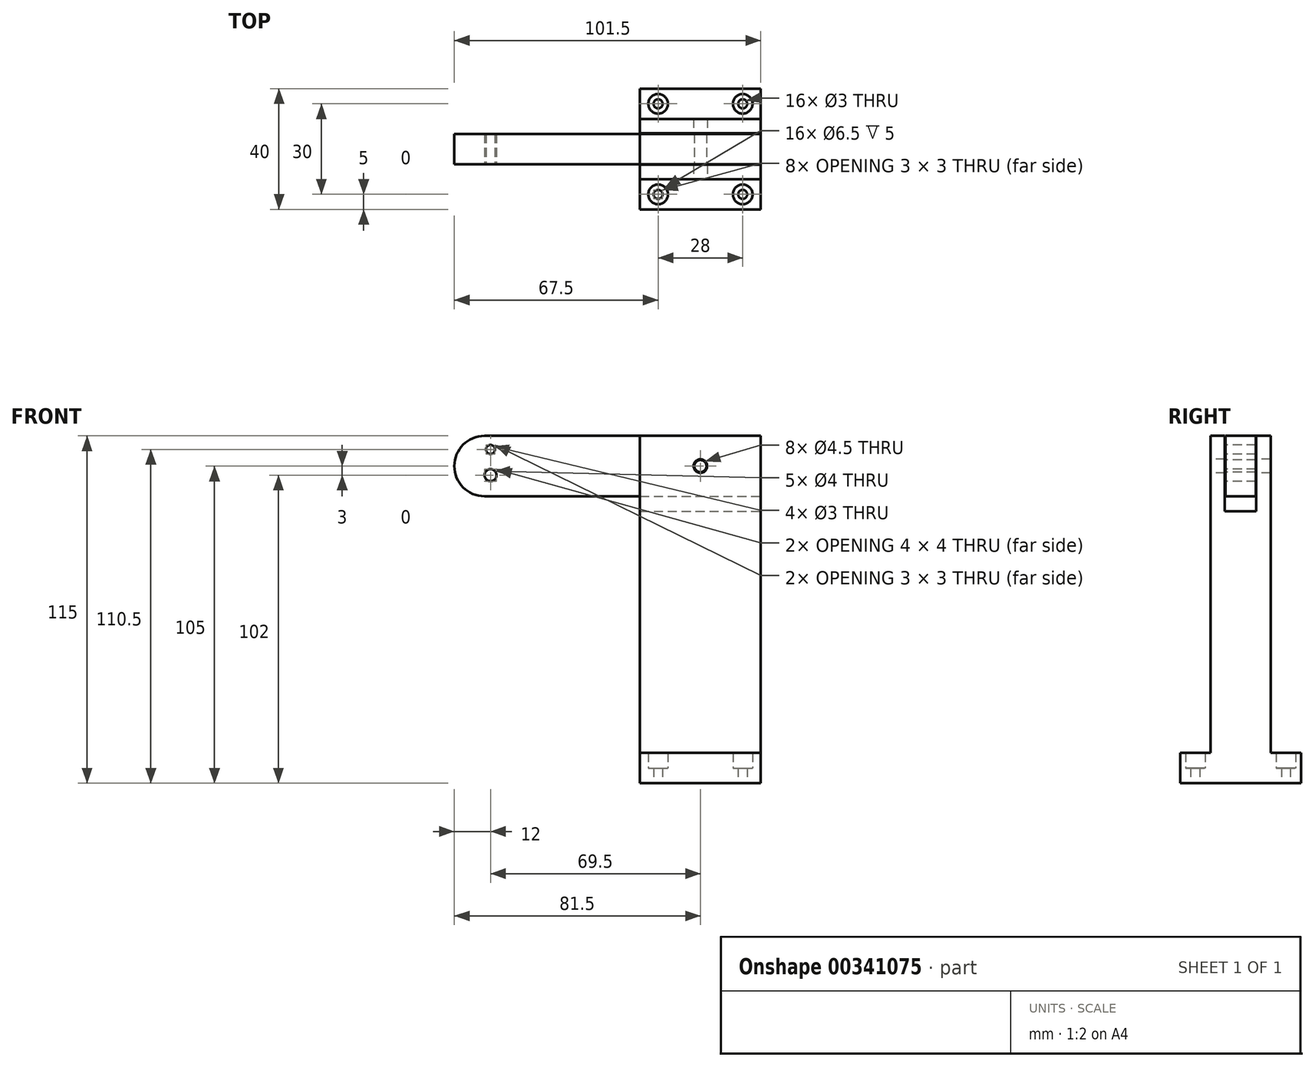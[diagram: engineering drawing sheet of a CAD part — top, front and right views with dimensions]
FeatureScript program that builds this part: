
annotation { "Feature Type Name" : "Feature", "Feature Type Description" : "" }
export const myFeature = defineFeature(function(context is Context, id is Id, definition is map)
    precondition{}
    {
        {
            var Q0;
            Q0=qCreatedBy(makeId("Top.planeOp"),FACE);
            var sketch = newSketch(context, id + "F0", { "sketchPlane" : qUnion([Q0])});
            skLineSegment(sketch, "E0.bottom", {"start": v(51.5, 0) * mm, "end": v(91.5, 0) * mm});
            skLineSegment(sketch, "E0.top", {"start": v(51.5, 40) * mm, "end": v(91.5, 40) * mm});
            skLineSegment(sketch, "E0.left", {"start": v(51.5, 0) * mm, "end": v(51.5, 40) * mm});
            skLineSegment(sketch, "E0.right", {"start": v(91.5, 0) * mm, "end": v(91.5, 40) * mm});
            skSolve(sketch);
        }
        {
            var Q0;
            Q0=qSketchRegion(id+"F0",true);
            extrude(context, id + "F1", {"entities" : qUnion([Q0]), "depth" : (95 + 20) * mm});
        }
        {
            var Q0;
            Q0=makeQuery(id+"F1.opExtrude","CAP_FACE",FACE,{"disambiguationData":[OSD([sQuery(id+"F0.wireOp",EDGE,"E0.bottom"),sQuery(id+"F0.wireOp",EDGE,"E0.top"),sQuery(id+"F0.wireOp",EDGE,"E0.left"),sQuery(id+"F0.wireOp",EDGE,"E0.right")])],"isStart":false});
            var sketch = newSketch(context, id + "F2", { "sketchPlane" : qUnion([Q0])});
            skLineSegment(sketch, "E1.bottom", {"start": v(51.5, 0) * mm, "end": v(91.5, 0) * mm});
            skLineSegment(sketch, "E1.top", {"start": v(51.5, 10) * mm, "end": v(91.5, 10) * mm});
            skLineSegment(sketch, "E1.left", {"start": v(51.5, 0) * mm, "end": v(51.5, 10) * mm});
            skLineSegment(sketch, "E1.right", {"start": v(91.5, 0) * mm, "end": v(91.5, 10) * mm});
            skLineSegment(sketch, "E2", {"start": v(51.5, 20) * mm, "end": v(91.5, 20) * mm, "construction": true});
            skLineSegment(sketch, "E3.MirrorCS", {"start": v(51.5, 30) * mm, "end": v(91.5, 30) * mm});
            skLineSegment(sketch, "E4.MirrorCS", {"start": v(51.5, 40) * mm, "end": v(51.5, 30) * mm});
            skLineSegment(sketch, "E5.MirrorCS", {"start": v(51.5, 40) * mm, "end": v(91.5, 40) * mm});
            skLineSegment(sketch, "E6.MirrorCS", {"start": v(91.5, 40) * mm, "end": v(91.5, 30) * mm});
            skSolve(sketch);
        }
        {
            var Q0;
            Q0=qSketchRegion(id+"F2",true);
            extrude(context, id + "F3", {"entities" : qUnion([Q0]), "operationType" : NewBodyOperationType.REMOVE, "oppositeDirection" : true, "depth" : (115 - 10) * mm});
        }
        {
            var Q0;
            Q0=makeQuery(id+"F3.boolean.opBoolean","COPY",FACE,{"derivedFrom":makeQuery(id+"F3.opExtrude","CAP_FACE",FACE,{"disambiguationData":[OSD([sQuery(id+"F2.wireOp",EDGE,"E1.bottom"),sQuery(id+"F2.wireOp",EDGE,"E1.top"),sQuery(id+"F2.wireOp",EDGE,"E1.left"),sQuery(id+"F2.wireOp",EDGE,"E1.right")])],"isStart":false})});
            var sketch = newSketch(context, id + "F4", { "sketchPlane" : qUnion([Q0])});
            skLineSegment(sketch, "E7", {"start": v(51.5, 20) * mm, "end": v(91.5, 20) * mm, "construction": true});
            skLineSegment(sketch, "E8", {"start": v(51.5, 20) * mm, "end": v(51.5, 35) * mm, "construction": true});
            skLineSegment(sketch, "E9", {"start": v(51.5, 35) * mm, "end": v(57.5, 35) * mm, "construction": true});
            skPoint(sketch, "E10", {"position": v(57.5, 35) * mm});
            skLineSegment(sketch, "E11", {"start": v(71.5, 20) * mm, "end": v(71.5, 42.68) * mm, "construction": true});
            skPoint(sketch, "E11.endSnap0", {"position": v(71.5, 30) * mm});
            skPoint(sketch, "E12.MirrorP", {"position": v(85.5, 35) * mm});
            skPoint(sketch, "E13.MirrorP", {"position": v(85.5, 5) * mm});
            skPoint(sketch, "E14.MirrorP", {"position": v(57.5, 5) * mm});
            skSolve(sketch);
        }
        {
            var Q0;
            Q0=sQuery(id+"F4.wireOp",VERTEX,"E14.MirrorP");
            var Q1;
            Q1=sQuery(id+"F4.wireOp",VERTEX,"E13.MirrorP");
            var Q2;
            Q2=sQuery(id+"F4.wireOp",VERTEX,"E12.MirrorP");
            var Q3;
            Q3=sQuery(id+"F4.wireOp",VERTEX,"E10");
            var Q4;
            Q4=makeQuery(id+"F1.opExtrude","SWEPT_BODY",BODY,{"disambiguationData":[OSD([sQuery(id+"F0.wireOp",EDGE,"E0.bottom"),sQuery(id+"F0.wireOp",EDGE,"E0.top"),sQuery(id+"F0.wireOp",EDGE,"E0.left"),sQuery(id+"F0.wireOp",EDGE,"E0.right")])]});
            hole(context, id + "F5", {"style" : HoleStyle.C_BORE, "endStyle" : HoleEndStyle.BLIND, "holeDiameter" : 3 * mm, "cBoreDiameter" : 6.5 * mm, "cBoreDepth" : 5 * mm, "holeDepth" : (10.4 + .3) * mm, "locations" : qUnion([Q0, Q1, Q2, Q3]), "scope" : qUnion([Q4])});
        }
        {
            var Q0;
            Q0=makeQuery(id+"F1.opExtrude","CAP_FACE",FACE,{"disambiguationData":[OSD([sQuery(id+"F0.wireOp",EDGE,"E0.bottom"),sQuery(id+"F0.wireOp",EDGE,"E0.top"),sQuery(id+"F0.wireOp",EDGE,"E0.left"),sQuery(id+"F0.wireOp",EDGE,"E0.right")])],"isStart":false});
            var sketch = newSketch(context, id + "F6", { "sketchPlane" : qUnion([Q0])});
            skLineSegment(sketch, "E15", {"start": v(51.5, 20) * mm, "end": v(91.5, 20) * mm, "construction": true});
            skLineSegment(sketch, "E16", {"start": v(51.5, 20) * mm, "end": v(51.5, 14.8) * mm});
            skLineSegment(sketch, "E17", {"start": v(51.5, 14.8) * mm, "end": v(91.5, 14.8) * mm});
            skLineSegment(sketch, "E18", {"start": v(91.5, 14.8) * mm, "end": v(91.5, 20) * mm});
            skLineSegment(sketch, "E19.MirrorCS", {"start": v(51.5, 20) * mm, "end": v(51.5, 25.2) * mm});
            skLineSegment(sketch, "E20.MirrorCS", {"start": v(51.5, 25.2) * mm, "end": v(91.5, 25.2) * mm});
            skLineSegment(sketch, "E21.MirrorCS", {"start": v(91.5, 25.2) * mm, "end": v(91.5, 20) * mm});
            skSolve(sketch);
        }
        {
            var Q0;
            Q0=qSketchRegion(id+"F6",true);
            extrude(context, id + "F7", {"entities" : qUnion([Q0]), "operationType" : NewBodyOperationType.REMOVE, "oppositeDirection" : true, "depth" : 25 * mm});
        }
        {
            var Q0;
            Q0=makeQuery(id+"F3.boolean.opBoolean","COPY",FACE,{"derivedFrom":makeQuery(id+"F3.opExtrude","SWEPT_FACE",FACE,{"disambiguationData":[OSD([sQuery(id+"F2.wireOp",EDGE,"E1.top")])]})});
            var sketch = newSketch(context, id + "F8", { "sketchPlane" : qUnion([Q0])});
            skLineSegment(sketch, "E22", {"start": v(71.5, 115) * mm, "end": v(71.5, 105) * mm, "construction": true});
            skCircle(sketch, "E23", {"center": v(71.5, 105) * mm, "radius": 2.25 * mm});
            skSolve(sketch);
        }
        {
            var Q0;
            Q0=qSketchRegion(id+"F8",true);
            extrude(context, id + "F9", {"entities" : qUnion([Q0]), "operationType" : NewBodyOperationType.REMOVE, "endBound" : BoundingType.THROUGH_ALL, "oppositeDirection" : true, "depth" : 25 * mm});
        }
        {
            var Q0;
            Q0=qCreatedBy(makeId("Top.planeOp"),FACE);
            cPlane(context, id + "F10", {"entities" : qUnion([Q0]), "cplaneType" : CPlaneType.OFFSET, "offset" : 105 * mm, "width" : 150 * mm, "height" : 150 * mm});
        }
        {
            var Q0;
            Q0=qCreatedBy(id+"F10.planeOp",FACE);
            var sketch = newSketch(context, id + "F11", { "sketchPlane" : qUnion([Q0])});
            skLineSegment(sketch, "E24", {"start": v(0, 0) * mm, "end": v(0, 20) * mm, "construction": true});
            skLineSegment(sketch, "E25", {"start": v(0, 20) * mm, "end": v(101.12, 20) * mm, "construction": true});
            skLineSegment(sketch, "E26.bottom", {"start": v(-10, 15) * mm, "end": v(91.5, 15) * mm});
            skLineSegment(sketch, "E26.top", {"start": v(-10, 25) * mm, "end": v(91.5, 25) * mm});
            skLineSegment(sketch, "E26.left", {"start": v(-10, 15) * mm, "end": v(-10, 25) * mm});
            skLineSegment(sketch, "E26.right", {"start": v(91.5, 15) * mm, "end": v(91.5, 25) * mm});
            skSolve(sketch);
        }
        {
            var Q0;
            Q0=qSketchRegion(id+"F11",true);
            extrude(context, id + "F12", {"entities" : qUnion([Q0]), "depth" : 20 * mm, "symmetric" : true});
        }
        {
            var Q0;
            Q0=makeQuery(id+"F12.opExtrude","SWEPT_FACE",FACE,{"disambiguationData":[OSD([sQuery(id+"F11.wireOp",EDGE,"E26.bottom")])]});
            var sketch = newSketch(context, id + "F13", { "sketchPlane" : qUnion([Q0])});
            skLineSegment(sketch, "E27", {"start": v(91.5, 115) * mm, "end": v(71.5, 115) * mm, "construction": true});
            skLineSegment(sketch, "E28", {"start": v(71.5, 115) * mm, "end": v(71.5, 105) * mm, "construction": true});
            skCircle(sketch, "E29", {"center": v(71.5, 105) * mm, "radius": 2 * mm});
            skLineSegment(sketch, "E30", {"start": v(-10, 95) * mm, "end": v(-10, 102) * mm, "construction": true});
            skLineSegment(sketch, "E31", {"start": v(-10, 102) * mm, "end": v(2, 102) * mm, "construction": true});
            skCircle(sketch, "E32", {"center": v(2, 102) * mm, "radius": 2 * mm});
            skLineSegment(sketch, "E33", {"start": v(2, 102) * mm, "end": v(2, 115) * mm, "construction": true});
            skCircle(sketch, "E34", {"center": v(2, 110.5) * mm, "radius": 1.5 * mm});
            skLineSegment(sketch, "E35", {"start": v(-10, 105) * mm, "end": v(38.14, 105) * mm, "construction": true});
            skArc(sketch, "E36", {"start": v(0, 115) * mm, "mid": v(-10, 105) * mm, "end": v(0, 95) * mm});
            skLineSegment(sketch, "E37", {"start": v(0, 115) * mm, "end": v(-10, 115) * mm});
            skLineSegment(sketch, "E38", {"start": v(-10, 115) * mm, "end": v(-10, 95) * mm});
            skLineSegment(sketch, "E39", {"start": v(-10, 95) * mm, "end": v(0, 95) * mm});
            skSolve(sketch);
        }
        {
            var Q0;
            Q0=qSketchRegion(id+"F13",true);
            extrude(context, id + "F14", {"entities" : qUnion([Q0]), "operationType" : NewBodyOperationType.REMOVE, "endBound" : BoundingType.THROUGH_ALL, "oppositeDirection" : true, "depth" : 25 * mm});
        }
    });
